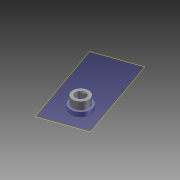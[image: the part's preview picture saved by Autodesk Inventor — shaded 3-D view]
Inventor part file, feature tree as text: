
AUTODESK INVENTOR PART (.ipt)
format: ipt  version: 2012 (Build 160160000, 160)  size: 116,736 bytes
history: native  units: mm
features: extrude x6, sketch x6, plane x1, reference x1, projected_geometry x1
ambient origin geometry x8: Origin, YZ Plane, XZ Plane, XY Plane, X Axis, Y Axis, Z Axis, Center Point
bodies: Solid1 (feature_tree)
feature tree (15):
  plane  "Work Plane1"
  extrude  "Extrusion4"  Depth=3.0mm TaperAngle=0.0deg
  extrude  "Extrusion5"  Depth=13.2mm
  extrude  "Extrusion10"  Depth=3.762mm
  extrude  "Extrusion12"  Depth=10.6mm
  extrude  "Extrusion13"  Depth=5.0mm TaperAngle=0.0deg
  extrude  "Extrusion14"  [1 undecoded]
  sketch  "Sketch5"  dims[d13=1.0mm d14=3.0mm d15=0.0mm]
  reference  "Reference1"
  sketch  "Sketch6"  dims[d16=0.3mm d17=0.0mm d26=13.2mm]
  sketch  "Sketch11"  dims[d27=6.6mm d28=3.762mm]
  sketch  "Sketch13"  dims[d29=2.7mm d30=0.0mm d33=10.6mm]
  sketch  "Sketch14"  dims[d34=5.0mm d35=0.0mm d36=5.0mm d37=0.0mm]
  projected_geometry  "Projected Loop5"
  sketch  "Sketch15"  dims[d38=0.5mm d39=0.0mm]
note: 1 required parameter value undecoded (feature->parameter linkage not recoverable at this tier; creation-order binding heuristic only, values carry confidence <= 0.55)
